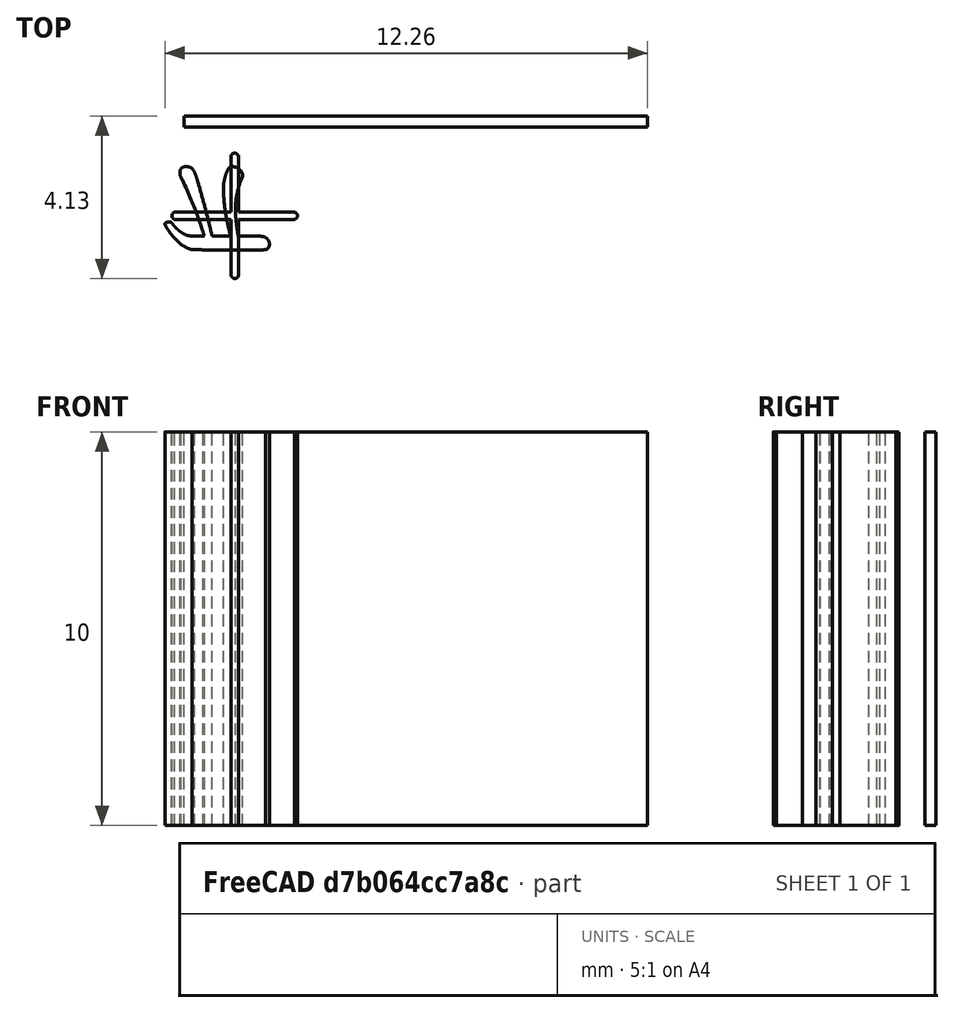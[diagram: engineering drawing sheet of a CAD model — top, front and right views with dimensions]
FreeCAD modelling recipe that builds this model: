
FCSTD DOCUMENT  (FreeCAD 0.19R)
Label: 3
License: All rights reserved
LicenseURL: http://en.wikipedia.org/wiki/All_rights_reserved
objects: Part::Feature×6, Sketcher::SketchObject×3, PartDesign::Pad×3, PartDesign::Body×3
note: 18 computed .brp shape members not serialized (recipe doc carries the construction recipe); baked Part::Feature solids carry a one-line shape summary decoded from their .brp

FEATURE [Part::Feature] MJX_13_TEX_I_3C0
  shape: bbox 2.653 x 2.116 x 2e-07 mm, 0 faces, 0 solids (baked)
FEATURE [Part::Feature] MJX_13_TEX_N_2B
  shape: bbox 3.189 x 3.184 x 2e-07 mm, 0 faces, 0 solids (baked)
FEATURE [Part::Feature] MJX_13_TEX_I_65
  shape: bbox 1.872 x 2.174 x 2e-07 mm, 0 faces, 0 solids (baked)
FEATURE [Part::Feature] MJX_13_TEX_I_65001
  shape: bbox 1.073 x 0.6943 x 2e-07 mm, 0 faces, 0 solids (baked)
FEATURE [Part::Feature] MJX_13_TEX_N_32
  shape: bbox 1.911 x 3.189 x 2e-07 mm, 0 faces, 0 solids (baked)
FEATURE [Part::Feature] Rectangle
  shape: bbox 11.77 x 0.2873 x 2e-07 mm, 0 faces, 0 solids (baked)
FEATURE [Sketcher::SketchObject] Sketch
  FullyConstrained = false
  MapMode = 5
  Support = -> [XY_Plane]
  sketch-geometry (42):
    g0: BSplineCurve PolesCount=3 KnotsCount=2 Degree=2 IsPeriodic=0
    g1: BSplineCurve PolesCount=2 KnotsCount=2 Degree=1 IsPeriodic=0
    g2: BSplineCurve PolesCount=2 KnotsCount=2 Degree=1 IsPeriodic=0
    g3: BSplineCurve PolesCount=3 KnotsCount=2 Degree=2 IsPeriodic=0
    g4: BSplineCurve PolesCount=2 KnotsCount=2 Degree=1 IsPeriodic=0
    g5: BSplineCurve PolesCount=2 KnotsCount=2 Degree=1 IsPeriodic=0
    g6: BSplineCurve PolesCount=3 KnotsCount=2 Degree=2 IsPeriodic=0
    g7: BSplineCurve PolesCount=3 KnotsCount=2 Degree=2 IsPeriodic=0
    g8: BSplineCurve PolesCount=3 KnotsCount=2 Degree=2 IsPeriodic=0
    g9: BSplineCurve PolesCount=3 KnotsCount=2 Degree=2 IsPeriodic=0
    g10: BSplineCurve PolesCount=3 KnotsCount=2 Degree=2 IsPeriodic=0
    g11: BSplineCurve PolesCount=3 KnotsCount=2 Degree=2 IsPeriodic=0
    g12: BSplineCurve PolesCount=3 KnotsCount=2 Degree=2 IsPeriodic=0
    g13: BSplineCurve PolesCount=3 KnotsCount=2 Degree=2 IsPeriodic=0
    g14: BSplineCurve PolesCount=3 KnotsCount=2 Degree=2 IsPeriodic=0
    g15: BSplineCurve PolesCount=3 KnotsCount=2 Degree=2 IsPeriodic=0
    g16: BSplineCurve PolesCount=3 KnotsCount=2 Degree=2 IsPeriodic=0
    g17: BSplineCurve PolesCount=3 KnotsCount=2 Degree=2 IsPeriodic=0
    g18: BSplineCurve PolesCount=3 KnotsCount=2 Degree=2 IsPeriodic=0
    g19: BSplineCurve PolesCount=3 KnotsCount=2 Degree=2 IsPeriodic=0
    g20: BSplineCurve PolesCount=3 KnotsCount=2 Degree=2 IsPeriodic=0
    g21: BSplineCurve PolesCount=2 KnotsCount=2 Degree=1 IsPeriodic=0
    g22: BSplineCurve PolesCount=2 KnotsCount=2 Degree=1 IsPeriodic=0
    g23: BSplineCurve PolesCount=3 KnotsCount=2 Degree=2 IsPeriodic=0
    g24: BSplineCurve PolesCount=3 KnotsCount=2 Degree=2 IsPeriodic=0
    g25: BSplineCurve PolesCount=3 KnotsCount=2 Degree=2 IsPeriodic=0
    g26: BSplineCurve PolesCount=3 KnotsCount=2 Degree=2 IsPeriodic=0
    g27: BSplineCurve PolesCount=3 KnotsCount=2 Degree=2 IsPeriodic=0
    g28: BSplineCurve PolesCount=3 KnotsCount=2 Degree=2 IsPeriodic=0
    g29: BSplineCurve PolesCount=3 KnotsCount=2 Degree=2 IsPeriodic=0
    g30: BSplineCurve PolesCount=3 KnotsCount=2 Degree=2 IsPeriodic=0
    g31: BSplineCurve PolesCount=3 KnotsCount=2 Degree=2 IsPeriodic=0
    g32: BSplineCurve PolesCount=3 KnotsCount=2 Degree=2 IsPeriodic=0
    g33: BSplineCurve PolesCount=3 KnotsCount=2 Degree=2 IsPeriodic=0
    g34: BSplineCurve PolesCount=3 KnotsCount=2 Degree=2 IsPeriodic=0
    g35: BSplineCurve PolesCount=3 KnotsCount=2 Degree=2 IsPeriodic=0
    g36: BSplineCurve PolesCount=2 KnotsCount=2 Degree=1 IsPeriodic=0
    g37: BSplineCurve PolesCount=2 KnotsCount=2 Degree=1 IsPeriodic=0
    g38: BSplineCurve PolesCount=3 KnotsCount=2 Degree=2 IsPeriodic=0
    g39: BSplineCurve PolesCount=3 KnotsCount=2 Degree=2 IsPeriodic=0
    g40: BSplineCurve PolesCount=3 KnotsCount=2 Degree=2 IsPeriodic=0
    g41: BSplineCurve PolesCount=3 KnotsCount=2 Degree=2 IsPeriodic=0
  constraints (42):
    c: Coincident(g0,g1)
    c: Coincident(g1,g2)
    c: Coincident(g2,g3)
    c: Coincident(g3,g4)
    c: Coincident(g4,g5)
    c: Coincident(g5,g6)
    c: Coincident(g6,g7)
    c: Coincident(g7,g8)
    c: Coincident(g8,g9)
    c: Coincident(g9,g10)
    c: Coincident(g10,g11)
    c: Coincident(g11,g12)
    c: Coincident(g12,g13)
    c: Coincident(g13,g14)
    c: Coincident(g14,g15)
    c: Coincident(g15,g16)
    c: Coincident(g16,g17)
    c: Coincident(g17,g18)
    c: Coincident(g18,g19)
    c: Coincident(g19,g20)
    c: Coincident(g20,g21)
    c: Coincident(g21,g22)
    c: Coincident(g22,g23)
    c: Coincident(g23,g24)
    c: Coincident(g24,g25)
    c: Coincident(g25,g26)
    c: Coincident(g26,g27)
    c: Coincident(g27,g28)
    c: Coincident(g28,g29)
    c: Coincident(g29,g30)
    c: Coincident(g30,g31)
    c: Coincident(g31,g32)
    c: Coincident(g32,g33)
    c: Coincident(g33,g34)
    c: Coincident(g34,g35)
    c: Coincident(g35,g36)
    c: Coincident(g36,g37)
    c: Coincident(g37,g38)
    c: Coincident(g38,g39)
    c: Coincident(g39,g40)
    c: Coincident(g40,g41)
    c: Coincident(g41,g0)
FEATURE [Sketcher::SketchObject] Sketch001
  FullyConstrained = false
  MapMode = 5
  Support = -> [XY_Plane002]
  sketch-geometry (21):
    g0: BSplineCurve PolesCount=2 KnotsCount=2 Degree=1 IsPeriodic=0
    g1: BSplineCurve PolesCount=3 KnotsCount=2 Degree=2 IsPeriodic=0
    g2: BSplineCurve PolesCount=2 KnotsCount=2 Degree=1 IsPeriodic=0
    g3: BSplineCurve PolesCount=2 KnotsCount=2 Degree=1 IsPeriodic=0
    g4: BSplineCurve PolesCount=2 KnotsCount=2 Degree=1 IsPeriodic=0
    g5: BSplineCurve PolesCount=3 KnotsCount=2 Degree=2 IsPeriodic=0
    g6: BSplineCurve PolesCount=3 KnotsCount=2 Degree=2 IsPeriodic=0
    g7: BSplineCurve PolesCount=2 KnotsCount=2 Degree=1 IsPeriodic=0
    g8: BSplineCurve PolesCount=2 KnotsCount=2 Degree=1 IsPeriodic=0
    g9: BSplineCurve PolesCount=3 KnotsCount=2 Degree=2 IsPeriodic=0
    g10: BSplineCurve PolesCount=3 KnotsCount=2 Degree=2 IsPeriodic=0
    g11: BSplineCurve PolesCount=2 KnotsCount=2 Degree=1 IsPeriodic=0
    g12: BSplineCurve PolesCount=2 KnotsCount=2 Degree=1 IsPeriodic=0
    g13: BSplineCurve PolesCount=3 KnotsCount=2 Degree=2 IsPeriodic=0
    g14: BSplineCurve PolesCount=2 KnotsCount=2 Degree=1 IsPeriodic=0
    g15: BSplineCurve PolesCount=2 KnotsCount=2 Degree=1 IsPeriodic=0
    g16: BSplineCurve PolesCount=3 KnotsCount=2 Degree=2 IsPeriodic=0
    g17: BSplineCurve PolesCount=2 KnotsCount=2 Degree=1 IsPeriodic=0
    g18: BSplineCurve PolesCount=2 KnotsCount=2 Degree=1 IsPeriodic=0
    g19: BSplineCurve PolesCount=3 KnotsCount=2 Degree=2 IsPeriodic=0
    g20: BSplineCurve PolesCount=2 KnotsCount=2 Degree=1 IsPeriodic=0
  constraints (21):
    c: Coincident(g0,g1)
    c: Coincident(g1,g2)
    c: Coincident(g2,g3)
    c: Coincident(g3,g4)
    c: Coincident(g4,g5)
    c: Coincident(g5,g6)
    c: Coincident(g6,g7)
    c: Coincident(g7,g8)
    c: Coincident(g8,g9)
    c: Coincident(g9,g10)
    c: Coincident(g10,g11)
    c: Coincident(g11,g12)
    c: Coincident(g12,g13)
    c: Coincident(g13,g14)
    c: Coincident(g14,g15)
    c: Coincident(g15,g16)
    c: Coincident(g16,g17)
    c: Coincident(g17,g18)
    c: Coincident(g18,g19)
    c: Coincident(g19,g20)
    c: Coincident(g20,g0)
FEATURE [Sketcher::SketchObject] Sketch002
  FullyConstrained = false
  MapMode = 5
  Support = -> [XY_Plane001]
  sketch-geometry (4):
    g0: BSplineCurve PolesCount=2 KnotsCount=2 Degree=1 IsPeriodic=0
    g1: BSplineCurve PolesCount=2 KnotsCount=2 Degree=1 IsPeriodic=0
    g2: BSplineCurve PolesCount=2 KnotsCount=2 Degree=1 IsPeriodic=0
    g3: BSplineCurve PolesCount=2 KnotsCount=2 Degree=1 IsPeriodic=0
  constraints (4):
    c: Coincident(g0,g1)
    c: Coincident(g1,g2)
    c: Coincident(g2,g3)
    c: Coincident(g3,g0)
FEATURE [PartDesign::Pad] Pad
  Direction = (1,1,1)
  Length = 10
  Length2 = 100
  Profile = -> Sketch
  Type = 0
FEATURE [PartDesign::Body] Body
  Group = -> [Sketch,Pad]
  Origin = -> Origin
  Tip = -> Pad
FEATURE [PartDesign::Pad] Pad001
  Direction = (1,1,1)
  Length = 10
  Length2 = 100
  Profile = -> Sketch002
  Type = 0
FEATURE [PartDesign::Body] Body001
  Group = -> [Sketch002,Pad001]
  Origin = -> Origin001
  Tip = -> Pad001
FEATURE [PartDesign::Pad] Pad002
  Direction = (1,1,1)
  Length = 10
  Length2 = 100
  Profile = -> Sketch001
  Type = 0
FEATURE [PartDesign::Body] Body002
  Group = -> [Sketch001,Pad002]
  Origin = -> Origin002
  Tip = -> Pad002
